# Revit family: Controls_BlueGiant_SP2
name_source: partatom
category: Specialty Equipment
units: mm (PartAtom-declared; Revit-internal decimal feet)

## family parameters
Always vertical = No
Cut with Voids When Loaded = No
Enable Cutting in Views = No
Maintain Annotation Orientation = No
Part Type = Normal
Room Calculation Point = No
Round Connector Dimension = Use Diameter
Shared = No
Work Plane-Based = Yes

## types (2) — shared parameters
Assembly Code = E1030300
Construction Details = http://www.arcat.com
Default Elevation = 4' - 0"
Green Building-LEED = http://www.arcat.com
Installation_Fabricaton = http://www.bluegiant.com
Keynote = 11160
MEP Amperage = 0 A
Manufacturer = Blue Giant Equipment Corp.
Manufacturer Fax = 905-457-2313
Manufacturer Website = http://www.bluegiant.com
Mounting Height = 5' - 6"
Panel Material = Metal - Blue Giant - Zinc Coated Steel
Product Data = http://www.arcat.com
Product Properties = http://www.arcat.com
Sales Information = http://www.bluegiant.com
Send Message = http://admin.arcat.com
SpecWizard = http://www.arcat.com
Specification = http://www.arcat.com
URL = http://www.bluegiant.com
Unit Depth = 0' - 4"
Unit Height = 0' - 8 1/2"
Unit Width = 0' - 6 1/2"
Voltage_MEP = 0 V
zero-valued in all types: Expected Lifespan (Years), Maintenance Schedule (Months), Warranty Duration (Years)

## per-type parameters (varying)
| type | AutoPark | Description | Model |
| With AutoPark Feature | Yes | Blue Giant SP2 Control Box with AutoPark | SP2-A |
| Basic | No | Blue Giant SP2 Control Box | SP2 |

## geometry (parser evidence)
native form markers: Blend x12, Sweep x4
no freeform markers — native parametric forms only
